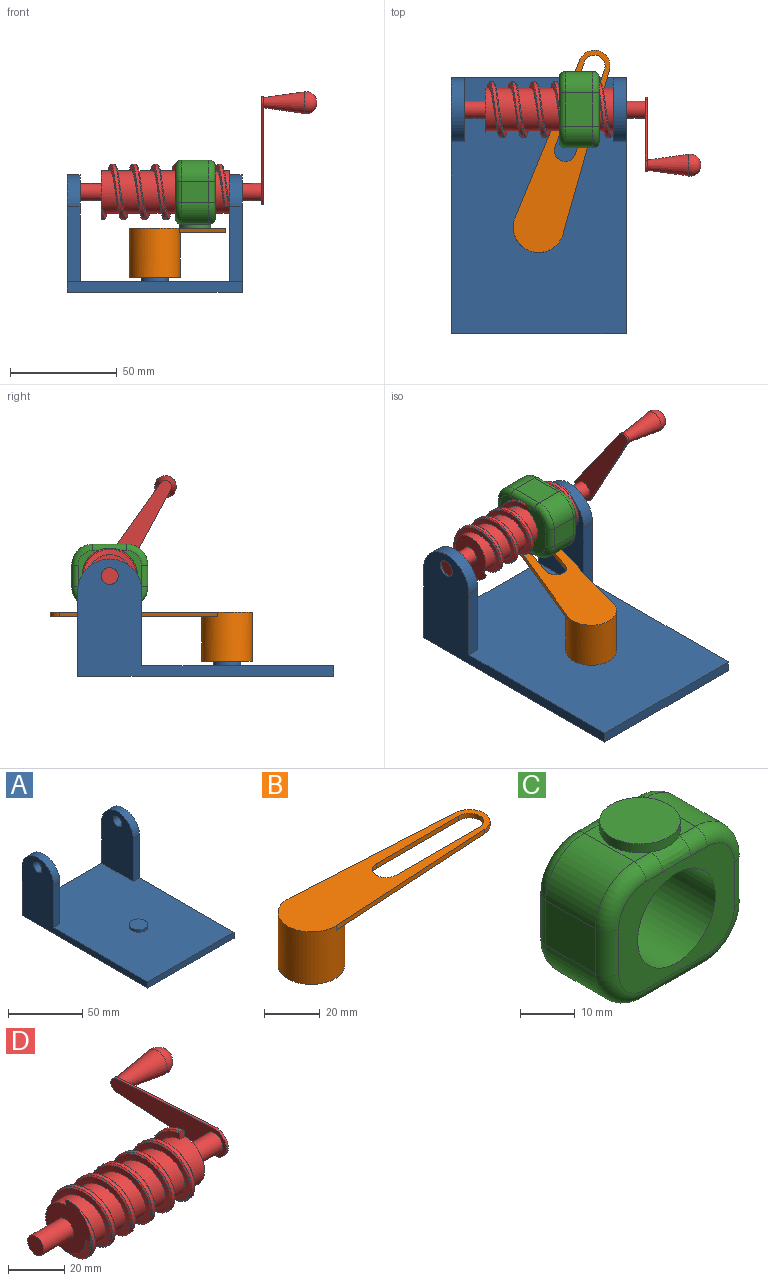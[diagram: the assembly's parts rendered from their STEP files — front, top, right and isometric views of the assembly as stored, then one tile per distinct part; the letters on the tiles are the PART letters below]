
ASSEMBLY  parts=4 mates=4
PART A: 16 faces, bbox 82x120x55 mm
  f0: plane 120x82mm, normal (0,0,1), area 9352.2mm2, adj f1,f2,f3,f4,f6,f8,f9,f10
  f1: plane 82x5mm, normal (0,-1,0), area 410mm2, adj f0,f2,f4,f5
  f2: plane 120x55mm, normal (1,0,0), area 1953.2mm2, adj f0,f1,f3,f5,f11,f12,f14
  f3: plane 82x40mm, normal (0,1,0), area 830mm2, adj f0,f2,f4,f5,f8,f10,f14,f15
  f4: plane 120x55mm, normal (-1,0,0), area 1953.2mm2, adj f0,f1,f3,f5,f9,f13,f15
  f5: plane 120x82mm, normal (0,0,-1), area 9840mm2, adj f1,f2,f3,f4
  f6: cylinder r=6.38mm len=12.76mm, axis (0,0,-1), area 80.1mm2, adj f0,f7
  f7: plane 12.76x12.76mm, normal (0,0,1), area 127.8mm2, adj f6
  f8: plane 50x30mm, normal (1,0,0), area 1353.2mm2, adj f0,f3,f9,f13,f15
  f9: plane 35x6mm, normal (0,-1,0), area 210mm2, adj f0,f4,f8,f15
  f10: plane 50x30mm, normal (-1,0,0), area 1353.2mm2, adj f0,f3,f11,f12,f14
  f11: plane 35x6mm, normal (0,-1,0), area 210mm2, adj f0,f2,f10,f14
  f12: cylinder r=4mm len=8mm, axis (1,0,0), area 150.8mm2, adj f2,f10
  f13: cylinder r=4mm len=8mm, axis (1,0,0), area 150.8mm2, adj f4,f8
  f14: cylinder r=15mm len=30mm, axis (1,0,0), area 282.7mm2, adj f2,f3,f10,f11
  f15: cylinder r=15mm len=30mm, axis (-1,0,0), area 282.7mm2, adj f3,f4,f8,f9
PART B: 11 faces, bbox 99.2x23.8x23 mm
  f0: plane 86.63x23.8mm, normal (0,0,-1), area 902.2mm2, adj f2,f4,f5,f6,f7,f8,f9,f10
  f1: plane 99.23x23.84mm, normal (0,0,1), area 1348.5mm2, adj f2,f4,f5,f6,f7,f8,f9,f10
  f2: cylinder r=11.92mm len=23.84mm, axis (0,0,-1), area 1650.4mm2, adj f0,f1,f3,f4,f6
  f3: plane 23.84x23.84mm, normal (0,0,-1), area 446.4mm2, adj f2
  f4: plane 79.73x4.6mm, normal (0.06,-1,0), area 159.7mm2, adj f0,f1,f2,f5
  f5: cylinder r=7.31mm len=14.6mm, axis (0,0,-1), area 44.3mm2, adj f0,f1,f4,f6
  f6: plane 79.73x4.6mm, normal (0.06,1,0), area 159.7mm2, adj f0,f1,f2,f5
  f7: plane 41.7x2mm, normal (0,-1,0), area 83.4mm2, adj f0,f1,f8,f10
  f8: cylinder r=5mm len=10mm, axis (0,0,1), area 31.4mm2, adj f0,f1,f7,f9
  f9: plane 42.17x2mm, normal (0,1,0), area 84.3mm2, adj f0,f1,f8,f10
  f10: cylinder r=5mm len=10mm, axis (0,0,1), area 32.3mm2, adj f0,f1,f7,f9
PART C: 34 faces, bbox 37.4x18.8x32.8 mm
  f0: plane 12.78x4.29mm, normal (0,0,1), area 20.9mm2, adj f8,f13,f14,f24
  f1: plane 29.78x24.16mm, normal (0,1,0), area 359.1mm2, adj f7,f14,f15,f16,f17,f18,f19,f20
  f2: plane 12.78x10mm, normal (-1,0,0), area 127.7mm2, adj f10,f12,f22,f31
  f3: plane 29.78x24.16mm, normal (0,-1,0), area 359.1mm2, adj f7,f24,f25,f26,f27,f28,f29,f30
  f4: plane 12.78x10mm, normal (1,0,0), area 127.7mm2, adj f11,f13,f17,f28
  f5: plane 12.78x4.29mm, normal (0,0,1), area 20.9mm2, adj f8,f12,f18,f27
  f6: plane 15.78x12.78mm, normal (0,0,-1), area 201.6mm2, adj f10,f11,f21,f32
  f7: cylinder r=10mm len=20mm, axis (0,-1,0), area 1179.7mm2, adj f1,f3
  f8: cylinder r=7.34mm len=14.67mm, axis (0,0,-1), area 92.2mm2, adj f0,f5,f9,f16,f25
  f9: plane 14.67x14.67mm, normal (0,0,1), area 169mm2, adj f8
  f10: cylinder r=10mm len=12.78mm, axis (0,-1,0), area 200.7mm2, adj f2,f6,f23,f33
  f11: cylinder r=10mm len=12.78mm, axis (0,1,0), area 200.7mm2, adj f4,f6,f19,f30
  f12: cylinder r=10mm len=12.78mm, axis (0,1,0), area 200.7mm2, adj f2,f5,f20,f29
  f13: cylinder r=10mm len=12.78mm, axis (0,-1,0), area 200.7mm2, adj f0,f4,f15,f26
  f14: cylinder r=3mm len=4.29mm, axis (1,0,0), area 20.2mm2, adj f0,f1,f15,f16
  f15: torus R=7mm, axis (0,1,0), area 66mm2, adj f1,f13,f14,f17
  f16: bspline ~8.36x3.37mm, area 29.3mm2, adj f1,f8,f14,f18
  f17: cylinder r=3mm len=10mm, axis (0,0,-1), area 47.1mm2, adj f1,f4,f15,f19
  f18: cylinder r=3mm len=4.29mm, axis (1,0,0), area 20.2mm2, adj f1,f5,f16,f20
  f19: torus R=7mm, axis (0,1,0), area 66mm2, adj f1,f11,f17,f21
  f20: torus R=7mm, axis (0,1,0), area 66mm2, adj f1,f12,f18,f22
  f21: cylinder r=3mm len=15.78mm, axis (-1,0,0), area 74.4mm2, adj f1,f6,f19,f23
  f22: cylinder r=3mm len=10mm, axis (0,0,1), area 47.1mm2, adj f1,f2,f20,f23
  f23: torus R=7mm, axis (0,1,0), area 66mm2, adj f1,f10,f21,f22
  f24: cylinder r=3mm len=4.29mm, axis (-1,0,0), area 20.2mm2, adj f0,f3,f25,f26
  f25: bspline ~9.16x3.81mm, area 29.3mm2, adj f3,f8,f24,f27
  f26: torus R=7mm, axis (0,1,0), area 66mm2, adj f3,f13,f24,f28
  f27: cylinder r=3mm len=4.29mm, axis (-1,0,0), area 20.2mm2, adj f3,f5,f25,f29
  f28: cylinder r=3mm len=10mm, axis (0,0,1), area 47.1mm2, adj f3,f4,f26,f30
  f29: torus R=7mm, axis (0,1,0), area 66mm2, adj f3,f12,f27,f31
  f30: torus R=7mm, axis (0,1,0), area 66mm2, adj f3,f11,f28,f32
  f31: cylinder r=3mm len=10mm, axis (0,0,-1), area 47.1mm2, adj f2,f3,f29,f33
  f32: cylinder r=3mm len=15.78mm, axis (1,0,0), area 74.4mm2, adj f3,f6,f30,f33
  f33: torus R=7mm, axis (0,1,0), area 66mm2, adj f3,f10,f31,f32
PART D: 21 faces, bbox 116x67.7x26.5 mm
  f0: cylinder r=13mm len=59.5mm, axis (-1,0,0), area -189.6mm2, adj f4,f17,f19,f20
  f1: bspline ~58.75x26mm, area 1023.8mm2, adj f2,f4,f17,f19
  f2: cylinder r=10mm len=60mm, axis (-1,0,0), area 2675.5mm2, adj f1,f3,f4,f17,f18
  f3: plane 20x20mm, normal (1,0,0), area 263.9mm2, adj f2,f7
  f4: plane 22.68x22.68mm, normal (-1,0,0), area 316mm2, adj f0,f1,f2,f6,f18,f19,f20
  f5: plane 8x8mm, normal (-1,0,0), area 50.3mm2, adj f6
  f6: cylinder r=4mm len=15mm, axis (-1,0,0), area 377mm2, adj f4,f5
  f7: cylinder r=4mm len=15mm, axis (-1,0,0), area 377mm2, adj f3,f13
  f8: cylinder r=5.88mm len=11.76mm, axis (-1,0,0), area 19.2mm2, adj f9,f11,f12,f13
  f9: plane 49.13x2.96mm, normal (0,0.06,-1), area 49.2mm2, adj f8,f10,f12,f13
  f10: cylinder r=2.92mm len=5.82mm, axis (-1,0,0), area 8.8mm2, adj f9,f11,f12,f13
  f11: plane 49.13x2.96mm, normal (0,0.06,1), area 49.2mm2, adj f8,f10,f12,f13
  f12: plane 58.11x11.76mm, normal (1,0,0), area 484.3mm2, adj f8,f9,f10,f11,f14
  f13: plane 58.11x11.76mm, normal (-1,0,0), area 452mm2, adj f7,f8,f9,f10,f11
  f14: cone r=2.39mm half-angle=8deg, axis (1,0,0), area 458.9mm2, adj f12,f16
  f15: plane 0.3x0.3mm, normal (1,0,0), area 0.1mm2, adj f16
  f16: torus R=0.15mm, axis (1,0,0), area 187.1mm2, adj f14,f15
  f17: plane 3x2.5mm, normal (0,-1,0), area 7.2mm2, adj f0,f1,f2,f18,f19,f20
  f18: bspline ~60x26mm, area 1072.9mm2, adj f2,f4,f17,f20
  f19: bspline ~58.5x26mm, area 333.8mm2, adj f0,f1,f4,f17
  f20: bspline ~60.5x26.5mm, area 341.9mm2, adj f0,f4,f17,f18
PLACE A t=(16.59,48.96,23.29)mm fixed
PLACE B rot(axis=(0,0,1),70.9deg) t=(30.67,43.06,30.29)mm
PLACE C rot(axis=(0.71,-0.71,0),180deg) t=(48.23,81.09,85.29)mm
PLACE D rot(axis=(1,0,0),121.9deg) t=(19.67,94.13,70.29)mm
MATE pin_slot C.f8 <-> B.f5  axis (0,0,-1) through (33.67,94.13,53.29)mm
MATE cylindrical C.f7 <-> D.f0  axis (1,0,0) through (43.06,94.13,70.29)mm
MATE revolute A.f12 <-> D.f0  axis (1,0,0) through (49.67,94.13,70.29)mm
MATE revolute A.f6 <-> B.f2  axis (0,0,1) through (14.67,39.13,30.29)mm
